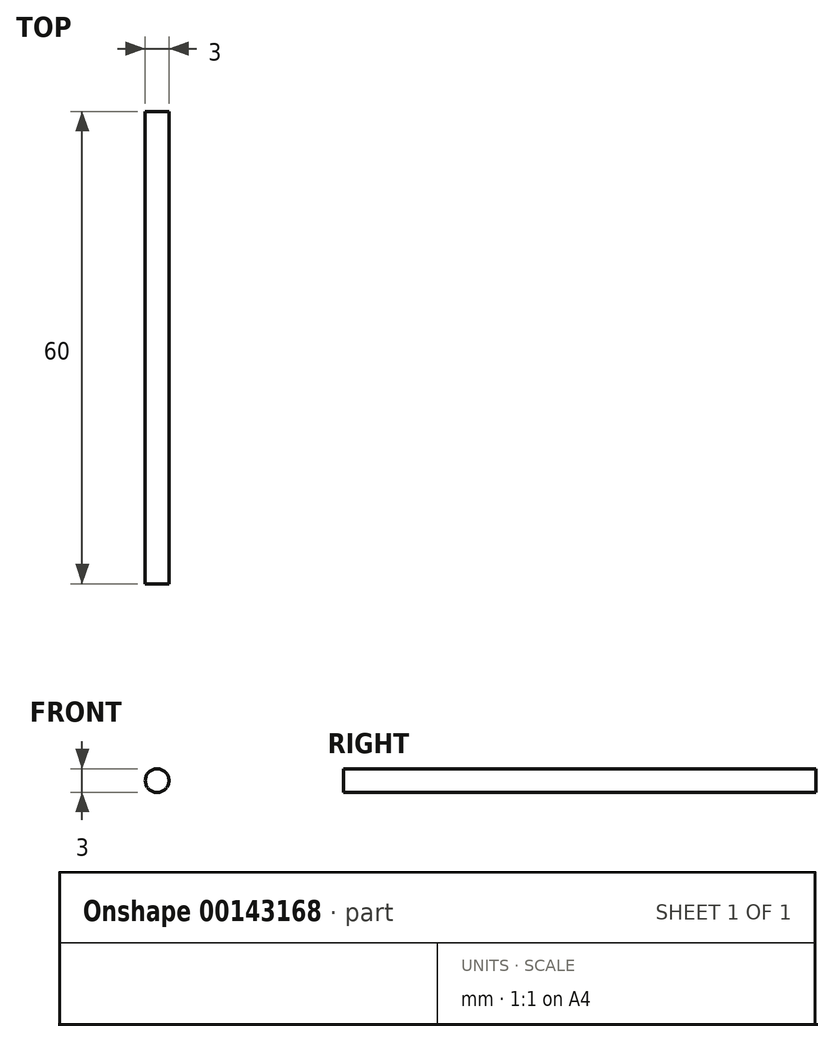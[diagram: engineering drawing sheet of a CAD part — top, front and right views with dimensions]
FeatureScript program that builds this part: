
annotation { "Feature Type Name" : "Feature", "Feature Type Description" : "" }
export const myFeature = defineFeature(function(context is Context, id is Id, definition is map)
    precondition{}
    {
        {
            var Q0;
            Q0=qCreatedBy(makeId("Front.planeOp"),FACE);
            var sketch = newSketch(context, id + "F0", { "sketchPlane" : qUnion([Q0])});
            skCircle(sketch, "E0", {"center": v(0, 0) * mm, "radius": 1.5 * mm});
            skSolve(sketch);
        }
        {
            var Q0;
            Q0 = qSketchRegion(id + "F0", true);
            extrude(context, id + "F1", {"entities" : qUnion([Q0]), "endBound" : BoundingType.SYMMETRIC, "depth" : 60 * mm});
        }
    });
